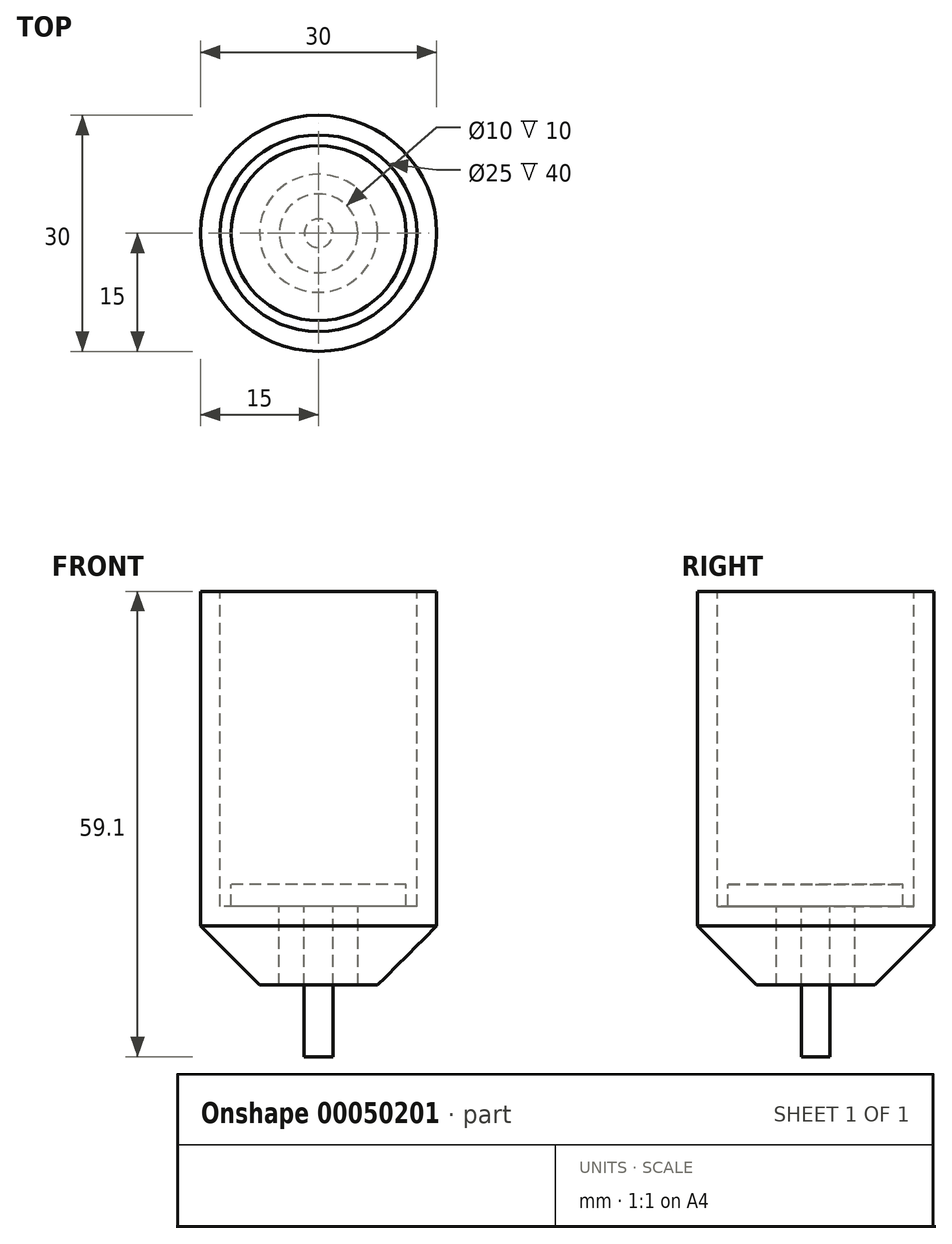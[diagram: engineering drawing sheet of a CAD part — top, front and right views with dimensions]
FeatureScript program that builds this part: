
annotation { "Feature Type Name" : "Feature", "Feature Type Description" : "" }
export const myFeature = defineFeature(function(context is Context, id is Id, definition is map)
    precondition{}
    {
        {
            var Q0;
            Q0=qCreatedBy(makeId("Front.planeOp"),FACE);
            var sketch = newSketch(context, id + "F0", { "sketchPlane" : qUnion([Q0])});
            skLineSegment(sketch, "E0", {"start": v(0, 35.07) * mm, "end": v(0, -33.14) * mm, "construction": true});
            skLineSegment(sketch, "E1", {"start": v(0, 25) * mm, "end": v(-15, 25) * mm});
            skLineSegment(sketch, "E2", {"start": v(-15, 25) * mm, "end": v(-15, -17.5) * mm});
            skLineSegment(sketch, "E3", {"start": v(-7.5, -25) * mm, "end": v(0, -25) * mm});
            skLineSegment(sketch, "E4", {"start": v(-5, -25) * mm, "end": v(-5, -15) * mm});
            skLineSegment(sketch, "E5", {"start": v(-5, -15) * mm, "end": v(-12.5, -15) * mm});
            skLineSegment(sketch, "E6", {"start": v(-12.5, -15) * mm, "end": v(-12.5, 25) * mm});
            skLineSegment(sketch, "E7", {"start": v(-15, -17.5) * mm, "end": v(-7.5, -25) * mm});
            skPoint(sketch, "E8.orphan", {"position": v(-15, -25) * mm});
            skSolve(sketch);
        }
        {
            var Q0;
            {var subQ2=sQuery(id+"F0.wireOp",EDGE,"E2");Q0=makeQuery(id+"F0.imprint","IMPRINT",FACE,{"disambiguationData":[TD([[makeQuery(id+"F0.imprint","IMPRINT",EDGE,{"derivedFrom":subQ2}),1.0]])]});}
            var Q1;
            Q1=sQuery(id+"F0.wireOp",EDGE,"E0");
            revolve(context, id + "F1", {"entities" : qUnion([Q0]), "axis" : qUnion([Q1]), "revolveType" : RevolveType.FULL});
        }
        {
            var Q0;
            Q0=qCreatedBy(makeId("Front.planeOp"),FACE);
            var sketch = newSketch(context, id + "F2", { "sketchPlane" : qUnion([Q0])});
            skLineSegment(sketch, "E9.0", {"start": v(-5, -15) * mm, "end": v(-11.11, -15) * mm});
            skLineSegment(sketch, "E10", {"start": v(0, -12.2) * mm, "end": v(0, -34.1) * mm});
            skLineSegment(sketch, "E11", {"start": v(0, -34.1) * mm, "end": v(-1.82, -34.1) * mm});
            skLineSegment(sketch, "E12", {"start": v(-1.82, -34.1) * mm, "end": v(-1.82, -15) * mm});
            skLineSegment(sketch, "E13", {"start": v(-1.82, -15) * mm, "end": v(-5, -15) * mm});
            skLineSegment(sketch, "E14", {"start": v(-11.11, -15) * mm, "end": v(-11.11, -12.2) * mm});
            skLineSegment(sketch, "E15", {"start": v(-11.11, -12.2) * mm, "end": v(0, -12.2) * mm});
            skPoint(sketch, "E16.orphan", {"position": v(-12.5, -15) * mm});
            skSolve(sketch);
        }
        {
            var Q0;
            Q0=makeQuery(id+"F2.imprint","IMPRINT",FACE,{"disambiguationData":[TD([[makeQuery(id+"F2.imprint","IMPRINT",EDGE,{"derivedFrom":sQuery(id+"F2.wireOp",EDGE,"E9.0")}),-1.0]])]});
            var Q1;
            Q1=sQuery(id+"F0.wireOp",EDGE,"E0");
            revolve(context, id + "F3", {"entities" : qUnion([Q0]), "axis" : qUnion([Q1]), "revolveType" : RevolveType.FULL});
        }
    });
